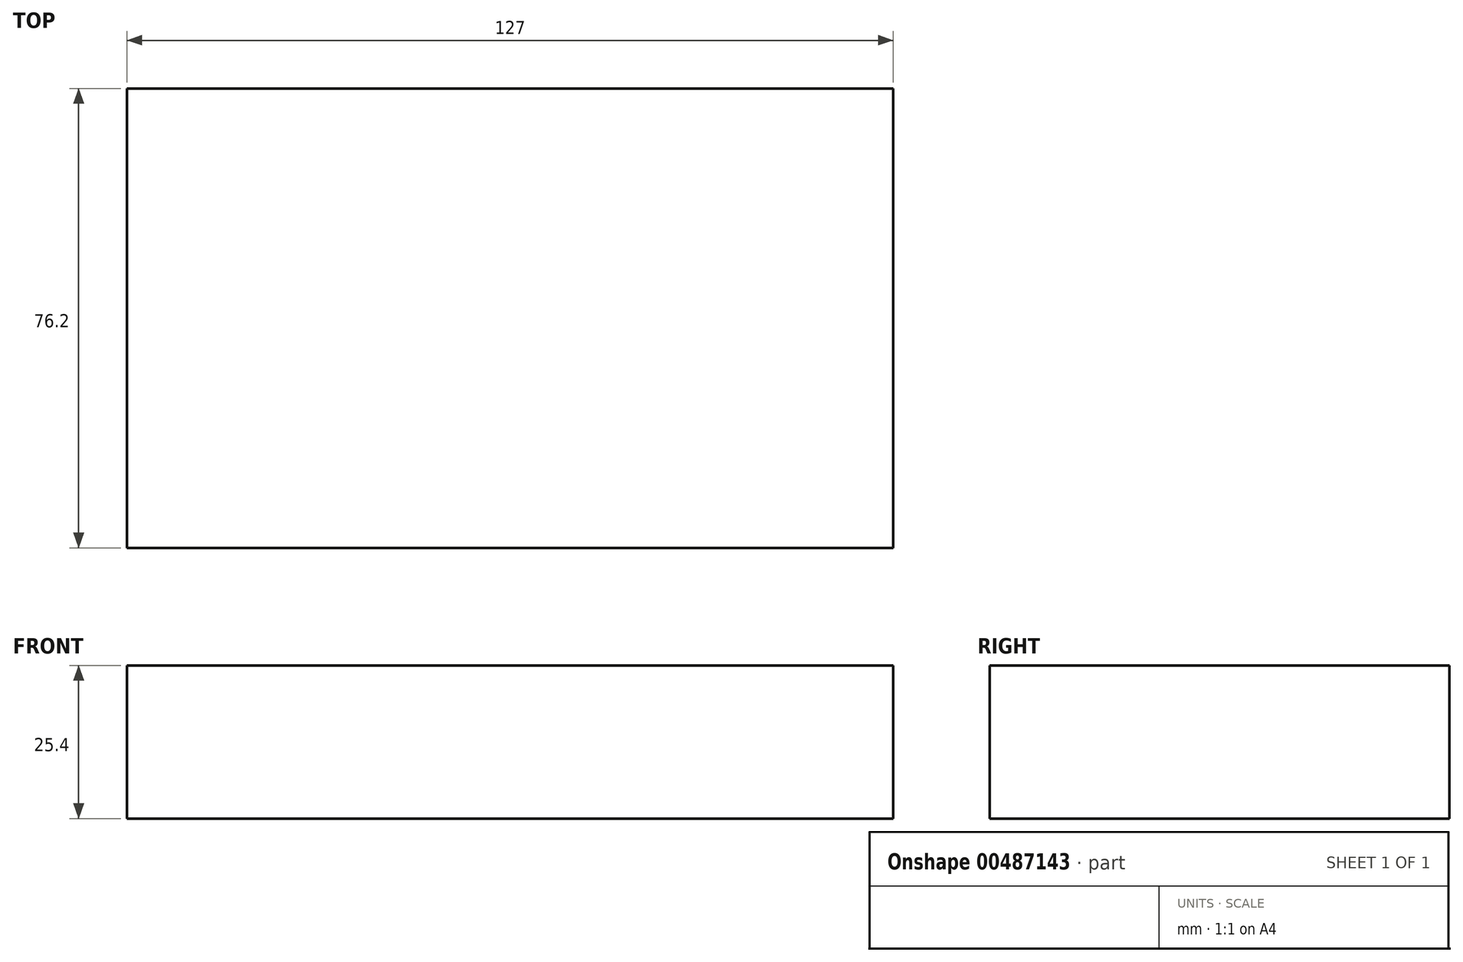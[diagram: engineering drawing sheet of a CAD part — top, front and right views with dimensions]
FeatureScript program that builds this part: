
annotation { "Feature Type Name" : "Feature", "Feature Type Description" : "" }
export const myFeature = defineFeature(function(context is Context, id is Id, definition is map)
    precondition{}
    {
        {
            var Q0;
            Q0=qCreatedBy(makeId("Top.planeOp"),FACE);
            var sketch = newSketch(context, id + "F0", { "sketchPlane" : qUnion([Q0])});
            skLineSegment(sketch, "E0.bottom", {"start": v(-75.32, 0) * mm, "end": v(51.68, 0) * mm});
            skLineSegment(sketch, "E0.top", {"start": v(-75.32, -76.2) * mm, "end": v(51.68, -76.2) * mm});
            skLineSegment(sketch, "E0.left", {"start": v(-75.32, 0) * mm, "end": v(-75.32, -76.2) * mm});
            skLineSegment(sketch, "E0.right", {"start": v(51.68, 0) * mm, "end": v(51.68, -76.2) * mm});
            skSolve(sketch);
        }
        {
            var Q0;
            Q0=makeQuery(id+"F0.imprint","IMPRINT",FACE,{"disambiguationData":[TD([[makeQuery(id+"F0.imprint","IMPRINT",EDGE,{"derivedFrom":sQuery(id+"F0.wireOp",EDGE,"E0.bottom")}),-1.0]])]});
            extrude(context, id + "F1", {"entities" : qUnion([Q0]), "depth" : 25.4 * mm});
        }
    });
